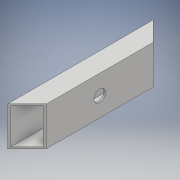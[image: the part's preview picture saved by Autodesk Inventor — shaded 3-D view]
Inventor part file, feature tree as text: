
AUTODESK INVENTOR PART (.ipt)
format: ipt  version: 2018 (Build 220112000, 112)  size: 111,616 bytes
history: native  units: mm
features: sketch x2, extrude x1, hole x1, chamfer x1
ambient origin geometry x8: Origin, YZ Plane, XZ Plane, XY Plane, X Axis, Y Axis, Z Axis, Center Point
bodies: Body1 (feature_tree)
feature tree (5):
  extrude  "押し出し2"  Depth=20.0mm
  hole  "穴2"  [1 undecoded]
  chamfer  "面取り1"  Distance=1.6mm
  sketch  "スケッチ2"
  sketch  "スケッチ5"
note: 1 required parameter value undecoded (feature->parameter linkage not recoverable at this tier; creation-order binding heuristic only, values carry confidence <= 0.55)
